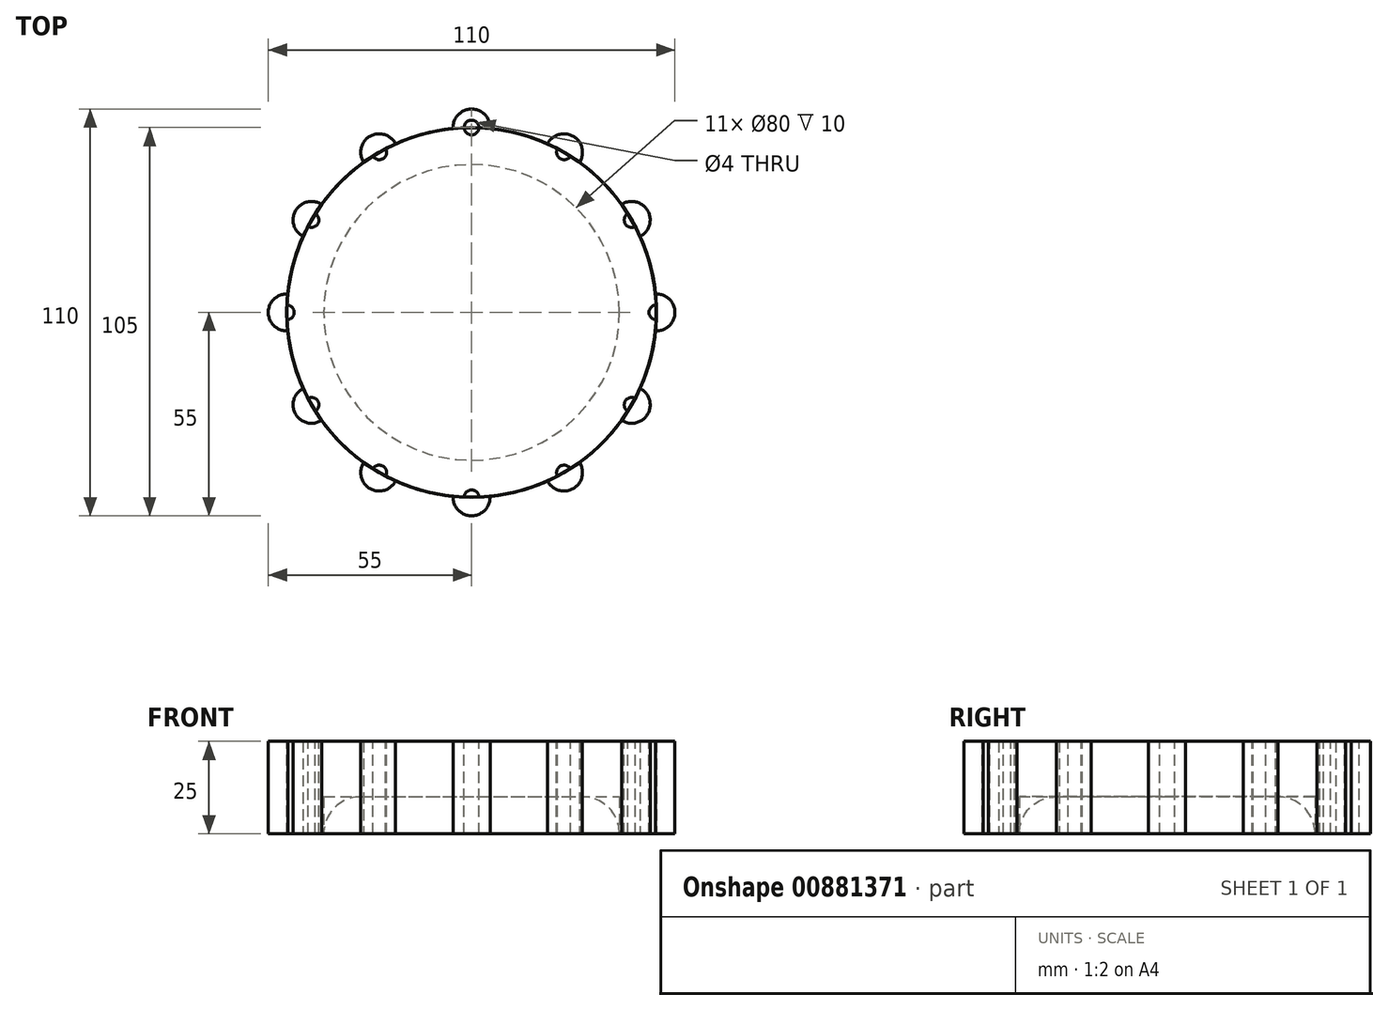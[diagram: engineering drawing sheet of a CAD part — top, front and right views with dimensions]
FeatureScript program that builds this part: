
annotation { "Feature Type Name" : "Feature", "Feature Type Description" : "" }
export const myFeature = defineFeature(function(context is Context, id is Id, definition is map)
    precondition{}
    {
        {
            var Q0;
            Q0=qCreatedBy(makeId("Top.planeOp"),FACE);
            var sketch = newSketch(context, id + "F0", { "sketchPlane" : qUnion([Q0])});
            skCircle(sketch, "E0", {"center": v(0, 0) * mm, "radius": 50 * mm});
            skCircle(sketch, "E1", {"center": v(0, 50) * mm, "radius": 5 * mm});
            skSolve(sketch);
        }
        {
            var Q0;
            {var subQ0=sQuery(id+"F0.wireOp",EDGE,"E1");var subQ1=sQuery(id+"F0.wireOp",EDGE,"E0");var subQ2=makeQuery(id+"F0.imprint","INTERSECT",VERTEX,{"disambiguationData":[OD(0.0)],"derivedFrom":[subQ1,subQ0]});Q0=makeQuery(id+"F0.imprint","IMPRINT",FACE,{"disambiguationData":[TD([[makeQuery(id+"F0.imprint","IMPRINT",EDGE,{"disambiguationData":[TD([[subQ2,-1.0]])],"derivedFrom":subQ1}),1.0]])]});}
            var Q1;
            {var subQ0=sQuery(id+"F0.wireOp",EDGE,"E1");var subQ1=sQuery(id+"F0.wireOp",EDGE,"E0");var subQ2=makeQuery(id+"F0.imprint","INTERSECT",VERTEX,{"disambiguationData":[OD(0.0)],"derivedFrom":[subQ1,subQ0]});Q1=makeQuery(id+"F0.imprint","IMPRINT",FACE,{"disambiguationData":[TD([[makeQuery(id+"F0.imprint","IMPRINT",EDGE,{"disambiguationData":[TD([[subQ2,1.0]])],"derivedFrom":subQ1}),1.0]])]});}
            var Q2;
            {var subQ0=sQuery(id+"F0.wireOp",EDGE,"E1");var subQ1=sQuery(id+"F0.wireOp",EDGE,"E0");var subQ2=makeQuery(id+"F0.imprint","INTERSECT",VERTEX,{"disambiguationData":[OD(0.0)],"derivedFrom":[subQ1,subQ0]});Q2=makeQuery(id+"F0.imprint","IMPRINT",FACE,{"disambiguationData":[TD([[makeQuery(id+"F0.imprint","IMPRINT",EDGE,{"disambiguationData":[TD([[subQ2,1.0]])],"derivedFrom":subQ1}),-1.0]])]});}
            extrude(context, id + "F1", {"entities" : qUnion([Q0, Q1, Q2]), "depth" : 25 * mm, "offsetDistance" : 25 * mm});
        }
        {
            var Q0;
            Q0=makeQuery(id+"F1.opExtrude","SWEPT_BODY",BODY,{"disambiguationData":[OSD([sQuery(id+"F0.wireOp",EDGE,"E0"),sQuery(id+"F0.wireOp",EDGE,"E1")])]});
            var Q1;
            Q1=makeQuery(id+"F1.opExtrude","SWEPT_FACE",FACE,{"disambiguationData":[OSD([sQuery(id+"F0.wireOp",EDGE,"E0")])]});
            circularPattern(context, id + "F2", {"entities" : qUnion([Q0]), "axis" : qUnion([Q1]), "angle" : 360 * degree, "instanceCount" : 12, "equalSpace" : true});
        }
        {
            var Q0;
            Q0=makeQuery(id+"F2.opPattern","COPY",FACE,{"derivedFrom":makeQuery(id+"F1.opExtrude","CAP_FACE",FACE,{"disambiguationData":[OSD([sQuery(id+"F0.wireOp",EDGE,"E0"),sQuery(id+"F0.wireOp",EDGE,"E1")])],"isStart":true}),"instanceName":"2"});
            var sketch = newSketch(context, id + "F3", { "sketchPlane" : qUnion([Q0])});
            skCircle(sketch, "E2", {"center": v(0, 0) * mm, "radius": 40 * mm});
            skSolve(sketch);
        }
        {
            var Q0;
            Q0=makeQuery(id+"F3.imprint","IMPRINT",FACE,{"disambiguationData":[TD([[makeQuery(id+"F3.imprint","IMPRINT",EDGE,{"derivedFrom":sQuery(id+"F3.wireOp",EDGE,"E2")}),1.0]])]});
            extrude(context, id + "F4", {"entities" : qUnion([Q0]), "operationType" : NewBodyOperationType.REMOVE, "oppositeDirection" : true, "depth" : 10 * mm, "offsetDistance" : 25 * mm});
        }
        {
            var Q0;
            Q0=makeQuery(id+"F4.boolean.opBoolean","COPY",EDGE,{"disambiguationData":[OD(0.0)],"derivedFrom":makeQuery(id+"F4.opExtrude","CAP_EDGE",EDGE,{"disambiguationData":[OSD([sQuery(id+"F3.wireOp",EDGE,"E2")])],"isStart":false})});
            fillet(context, id + "F5", {"entities" : qUnion([Q0]), "radius" : 10 * mm, "tangentPropagation" : true, "allowEdgeOverflow" : false});
        }
        {
            var Q0;
            Q0=makeQuery(id+"F1.opExtrude","CAP_FACE",FACE,{"disambiguationData":[OSD([sQuery(id+"F0.wireOp",EDGE,"E0"),sQuery(id+"F0.wireOp",EDGE,"E1")])],"isStart":false});
            var sketch = newSketch(context, id + "F6", { "sketchPlane" : qUnion([Q0])});
            skPoint(sketch, "E3", {"position": v(0, 50) * mm});
            skPoint(sketch, "E4", {"position": v(0, -50) * mm});
            skPoint(sketch, "E5", {"position": v(50, 0) * mm});
            skPoint(sketch, "E6", {"position": v(-50, 0) * mm});
            skPoint(sketch, "E7", {"position": v(-43.3, 25) * mm});
            skPoint(sketch, "E8", {"position": v(-25, 43.3) * mm});
            skPoint(sketch, "E9", {"position": v(-43.3, -25) * mm});
            skPoint(sketch, "E10", {"position": v(-25, -43.3) * mm});
            skPoint(sketch, "E11", {"position": v(25, -43.3) * mm});
            skPoint(sketch, "E12", {"position": v(43.3, -25) * mm});
            skPoint(sketch, "E13", {"position": v(43.3, 25) * mm});
            skPoint(sketch, "E14", {"position": v(25, 43.3) * mm});
            skSolve(sketch);
        }
        {
            var Q0;
            Q0=sQuery(id+"F6.wireOp",VERTEX,"E14");
            var Q1;
            Q1=sQuery(id+"F6.wireOp",VERTEX,"E13");
            var Q2;
            Q2=sQuery(id+"F6.wireOp",VERTEX,"E5");
            var Q3;
            Q3=sQuery(id+"F6.wireOp",VERTEX,"E12");
            var Q4;
            Q4=sQuery(id+"F6.wireOp",VERTEX,"E11");
            var Q5;
            Q5=sQuery(id+"F6.wireOp",VERTEX,"E4");
            var Q6;
            Q6=sQuery(id+"F6.wireOp",VERTEX,"E10");
            var Q7;
            Q7=sQuery(id+"F6.wireOp",VERTEX,"E9");
            var Q8;
            Q8=sQuery(id+"F6.wireOp",VERTEX,"E6");
            var Q9;
            Q9=sQuery(id+"F6.wireOp",VERTEX,"E7");
            var Q10;
            Q10=sQuery(id+"F6.wireOp",VERTEX,"E8");
            var Q11;
            Q11=sQuery(id+"F6.wireOp",VERTEX,"E3");
            var Q12;
            Q12=makeQuery(id+"F1.opExtrude","SWEPT_BODY",BODY,{"disambiguationData":[OSD([sQuery(id+"F0.wireOp",EDGE,"E0"),sQuery(id+"F0.wireOp",EDGE,"E1")])]});
            hole(context, id + "F7", {"style" : HoleStyle.SIMPLE, "endStyle" : HoleEndStyle.THROUGH, "holeDiameter" : 4 * mm, "majorDiameter" : 5 * mm, "isTappedThrough" : true, "tappedDepth" : 12 * mm, "tapClearance" : 3, "locations" : qUnion([Q0, Q1, Q2, Q3, Q4, Q5, Q6, Q7, Q8, Q9, Q10, Q11]), "scope" : qUnion([Q12])});
        }
    });
